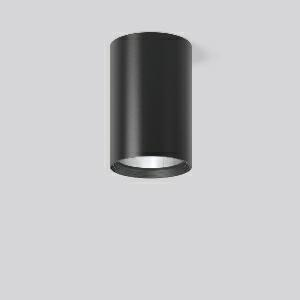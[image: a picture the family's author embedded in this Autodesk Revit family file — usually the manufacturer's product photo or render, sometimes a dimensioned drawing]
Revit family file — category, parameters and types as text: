
# Revit family: heledon_maxi_a_931232_003_a989
name_source: partatom
category: Lighting Fixtures
units: mm (PartAtom-declared; Revit-internal decimal feet)

## family parameters
Cut with Voids When Loaded = No
Host = Face
Light Source = No
Part Type = Normal
Room Calculation Point = No
Round Connector Dimension = Use Diameter
Shared = No

## types (1)
- HELEDON maxi A (1 x LED Modul 932 fresh meat, 2150 lm, 3200)
    Apparent Load = 33 VA
    Approval mark = CE
    CIE Flux Codes = 100 100 100 100 100
    Color Rendering = 90
    Color Temperature = 3200
    Default Elevation = 1800 mm
    Description = Series: HELEDON maxi
Cylindrical surface-mounted downlight. Housing: die-cast aluminium, powder-coated. Internal ceiling frame polycarbonate with bayonet mounting. Black plastic ring and recessed LED to prevent glare from the side. Optical assembly with reflector made of MIRO-Silver with 98% total light reflection for outstanding efficiency - can be changed without tools. Special LED for illumination of meat included. Suitable for Ceiling mounting. Easy installation with a separate ceiling frame with bayonet mounting and plug connection. Driver integrated. Connected via plug-in connector. High quality converter without flickering and stroboscopic effect. The following accessories can be mounted without use of tools: interchangeable lenses, decorative glasses, honeycomb louvre, clear and frosted diffusers, white interchangeable plastic ring. 
Colour: deep black, matt (RAL 9005)
Diameter: 123 mm
Height: 183 mm
Lamp: LED
Socket: without socket
Colour temperature: fresh meat
System power: 33 W
Rated luminous flux: 2150 lm
Luminous efficiency: 65 lm/W
Control gear: Regulated power supply
Protection class: I
Type of protection: IP 20
    Height = 183 mm
    Lamp = 1 x LED Modul 932 fresh meat
    Lamp Light Flux = 2150 lm
    Lamp count = 1
    Length = 123 mm
    Lifetime = 50000 h
    Luminous efficacy = 65 lm/W
    Manufacturer = RZB
    ModVariant = No
    Model = 931232.003
    Mounting Place = Ceiling
    Mounting Type = Surface mounted
    Number of Poles = 1
    OnlyDefault = Yes
    Power Factor = 1
    Product Name = HELEDON maxi A
    Product group = Surface mounted downlights
    ProductGroupID = 302
    Protection Class = Protection class I
    Protection Degree = IP 20
    RLX_Detail_Level = 1
    RLX_Emergency_Light_Flux = 0 lm
    RLX_Emergency_Type = 0
    RLX_Emergency_Type_DB = No
    RlxData = <blob elided: 97645 chars, md5=0e12a6eb>
    Socket = socket
    Standby Power = 0 W
    System Light Flux = 2150 lm
    System Power = 33 W
    Type Comments = Product without accessories
    Type Image = 931192.003.jpg
    URL = http://relux.com
    VarID = ---
    Voltage = 230 V
    Voltage Range = 220-240 V
    Weight = 0.00 kg
    Width = 0 mm  [stored 0 ft]

note: [stored X ft] marks values corroborated as IEEE doubles in the binary element streams (Revit-internal decimal feet)

## geometry (parser evidence)
native form markers: Blend x4, Sweep x10
no freeform markers — native parametric forms only
